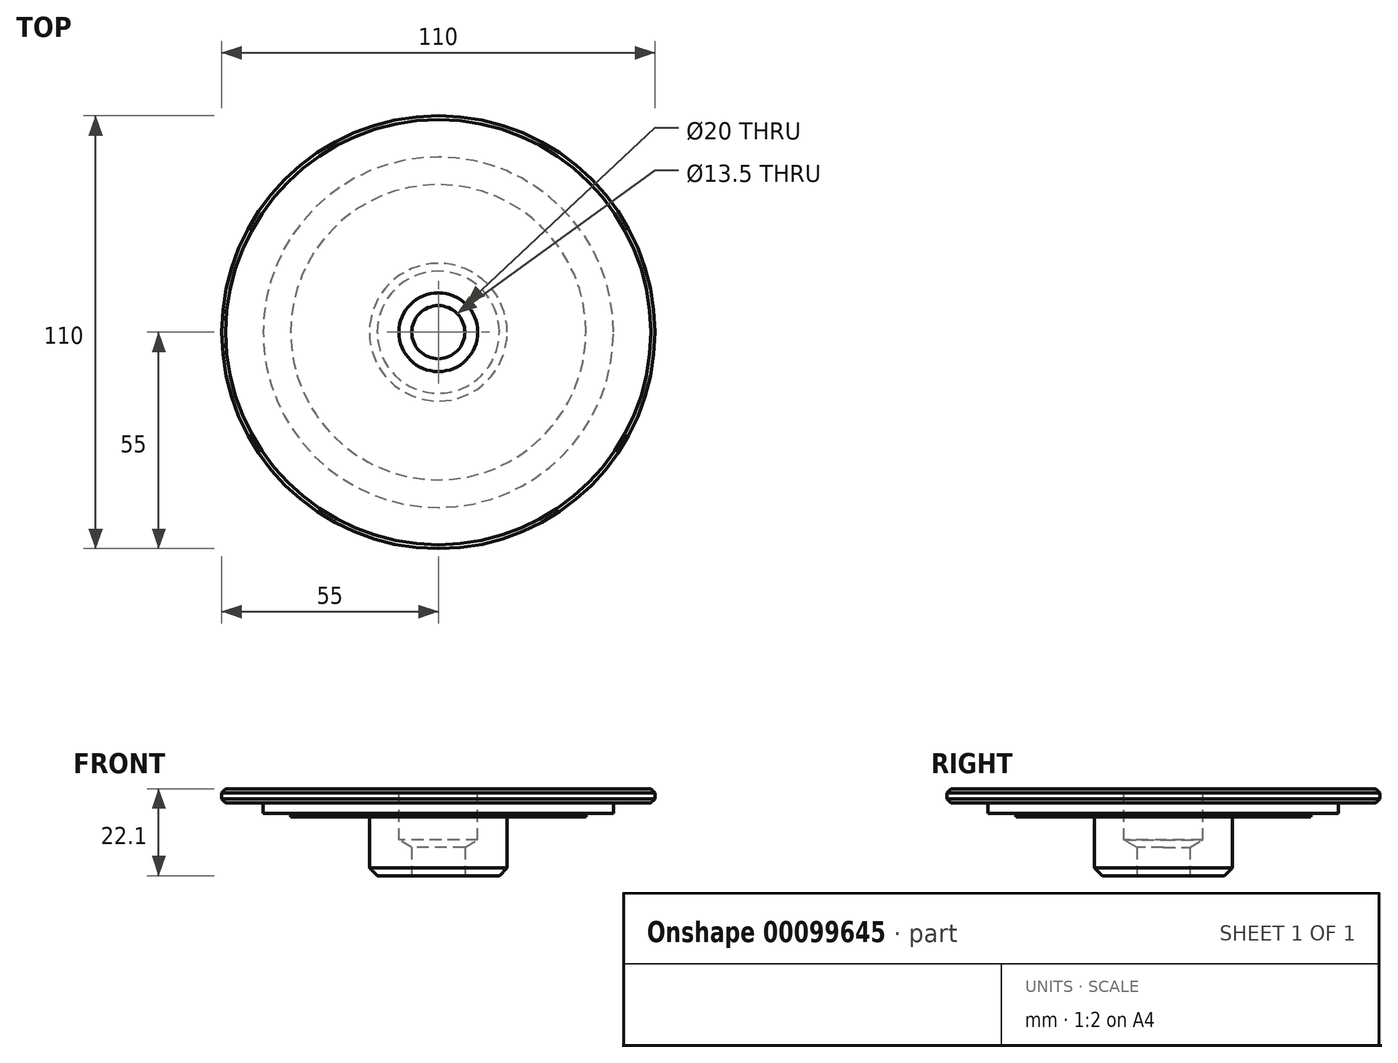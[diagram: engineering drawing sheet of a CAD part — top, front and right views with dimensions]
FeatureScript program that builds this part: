
annotation { "Feature Type Name" : "Feature", "Feature Type Description" : "" }
export const myFeature = defineFeature(function(context is Context, id is Id, definition is map)
    precondition{}
    {
        {
            var Q0;
            Q0=qCreatedBy(makeId("Top.planeOp"),FACE);
            var sketch = newSketch(context, id + "F0", { "sketchPlane" : qUnion([Q0])});
            skCircle(sketch, "E0", {"center": v(0, 0) * mm, "radius": 55 * mm});
            skSolve(sketch);
        }
        {
            var Q0;
            Q0 = qSketchRegion(id + "F0", true);
            extrude(context, id + "F1", {"entities" : qUnion([Q0]), "oppositeDirection" : true, "depth" : 3.6 * mm});
        }
        {
            var Q0;
            Q0=makeQuery(id+"F1.opExtrude","CAP_FACE",FACE,{"disambiguationData":[OSD([sQuery(id+"F0.wireOp",EDGE,"E0")])],"isStart":false});
            var sketch = newSketch(context, id + "F2", { "sketchPlane" : qUnion([Q0])});
            skCircle(sketch, "E1", {"center": v(0, 0) * mm, "radius": 44.5 * mm});
            skSolve(sketch);
        }
        {
            var Q0;
            Q0 = qSketchRegion(id + "F2", true);
            extrude(context, id + "F3", {"entities" : qUnion([Q0]), "operationType" : NewBodyOperationType.ADD, "depth" : 2.7 * mm});
        }
        {
            var Q0;
            Q0=makeQuery(id+"F3.opExtrude","CAP_FACE",FACE,{"disambiguationData":[OSD([sQuery(id+"F2.wireOp",EDGE,"E1")])],"isStart":false});
            var sketch = newSketch(context, id + "F4", { "sketchPlane" : qUnion([Q0])});
            skCircle(sketch, "E2", {"center": v(0, 0) * mm, "radius": 37.5 * mm});
            skSolve(sketch);
        }
        {
            var Q0;
            Q0 = qSketchRegion(id + "F4", true);
            extrude(context, id + "F5", {"entities" : qUnion([Q0]), "operationType" : NewBodyOperationType.ADD, "depth" : 0.8 * mm});
        }
        {
            var Q0;
            Q0=makeQuery(id+"F5.opExtrude","CAP_FACE",FACE,{"disambiguationData":[OSD([sQuery(id+"F4.wireOp",EDGE,"E2")])],"isStart":false});
            var sketch = newSketch(context, id + "F6", { "sketchPlane" : qUnion([Q0])});
            skCircle(sketch, "E3", {"center": v(0, 0) * mm, "radius": 17.5 * mm});
            skSolve(sketch);
        }
        {
            var Q0;
            Q0 = qSketchRegion(id + "F6", true);
            extrude(context, id + "F7", {"entities" : qUnion([Q0]), "operationType" : NewBodyOperationType.ADD, "depth" : 15 * mm});
        }
        {
            var Q0;
            Q0=makeQuery(id+"F7.opExtrude","CAP_EDGE",EDGE,{"disambiguationData":[OSD([sQuery(id+"F6.wireOp",EDGE,"E3")])],"isStart":false});
            chamfer(context, id + "F8", {"entities" : qUnion([Q0]), "width" : 2 * mm, "tangentPropagation" : true});
        }
        {
            var Q0;
            Q0=makeQuery(id+"F1.opExtrude","CAP_FACE",FACE,{"disambiguationData":[OSD([sQuery(id+"F0.wireOp",EDGE,"E0")])],"isStart":true});
            var sketch = newSketch(context, id + "F9", { "sketchPlane" : qUnion([Q0])});
            skCircle(sketch, "E4", {"center": v(0, 0) * mm, "radius": 10 * mm});
            skSolve(sketch);
        }
        {
            var Q0;
            Q0=sQuery(id+"F9.wireOp",VERTEX,"E4.center");
            var Q1;
            Q1=makeQuery(id+"F1.opExtrude","SWEPT_BODY",BODY,{"disambiguationData":[OSD([sQuery(id+"F0.wireOp",EDGE,"E0")])]});
            hole(context, id + "F10", {"style" : HoleStyle.SIMPLE, "endStyle" : HoleEndStyle.BLIND, "holeDiameter" : 20 * mm, "holeDepth" : 13 * mm, "startFromSketch" : true, "locations" : qUnion([Q0]), "scope" : qUnion([Q1])});
        }
        {
            var Q0;
            Q0=makeQuery(id+"F7.opExtrude","CAP_FACE",FACE,{"disambiguationData":[OSD([sQuery(id+"F6.wireOp",EDGE,"E3")])],"isStart":false});
            var sketch = newSketch(context, id + "F11", { "sketchPlane" : qUnion([Q0])});
            skSolve(sketch);
        }
        {
            var Q0;
            {var subQ0=sQuery(id+"F6.wireOp",EDGE,"E3");Q0=makeQuery(id+"F11.imprint","IMPRINT",FACE,{"disambiguationData":[TD([[makeQuery(id+"F11.imprint","IMPRINT",EDGE,{"derivedFrom":makeQuery(id+"F8.opChamfer","BLEND_EDGE",EDGE,{"blendedFrom":[makeQuery(id+"F7.opExtrude","CAP_EDGE",EDGE,{"disambiguationData":[OSD([subQ0])],"isStart":false}),makeQuery(id+"F7.opExtrude","CAP_FACE",FACE,{"disambiguationData":[OSD([subQ0])],"isStart":false})],"blendedInto":[makeQuery(id+"F7.opExtrude","CAP_FACE",FACE,{"disambiguationData":[OSD([subQ0])],"isStart":false})]})}),1.0]])]});}
            var sketch = newSketch(context, id + "F12", { "sketchPlane" : qUnion([Q0])});
            skCircle(sketch, "E5", {"center": v(0, 0) * mm, "radius": 6.75 * mm});
            skSolve(sketch);
        }
        {
            var Q0;
            Q0=sQuery(id+"F12.wireOp",VERTEX,"E5.center");
            var Q1;
            Q1=makeQuery(id+"F1.opExtrude","SWEPT_BODY",BODY,{"disambiguationData":[OSD([sQuery(id+"F0.wireOp",EDGE,"E0")])]});
            hole(context, id + "F13", {"style" : HoleStyle.SIMPLE, "endStyle" : HoleEndStyle.THROUGH, "holeDiameter" : 13.5 * mm, "startFromSketch" : true, "locations" : qUnion([Q0]), "scope" : qUnion([Q1]), "isTappedThrough" : true});
        }
        {
            var Q0;
            Q0=makeQuery(id+"F1.opExtrude","CAP_EDGE",EDGE,{"disambiguationData":[OSD([sQuery(id+"F0.wireOp",EDGE,"E0")])],"isStart":true});
            chamfer(context, id + "F14", {"entities" : qUnion([Q0]), "width" : 1 * mm, "tangentPropagation" : true});
        }
        {
            var Q0;
            Q0=makeQuery(id+"F1.opExtrude","CAP_EDGE",EDGE,{"disambiguationData":[OSD([sQuery(id+"F0.wireOp",EDGE,"E0")])],"isStart":false});
            chamfer(context, id + "F15", {"entities" : qUnion([Q0]), "width" : 1 * mm, "tangentPropagation" : true});
        }
    });
